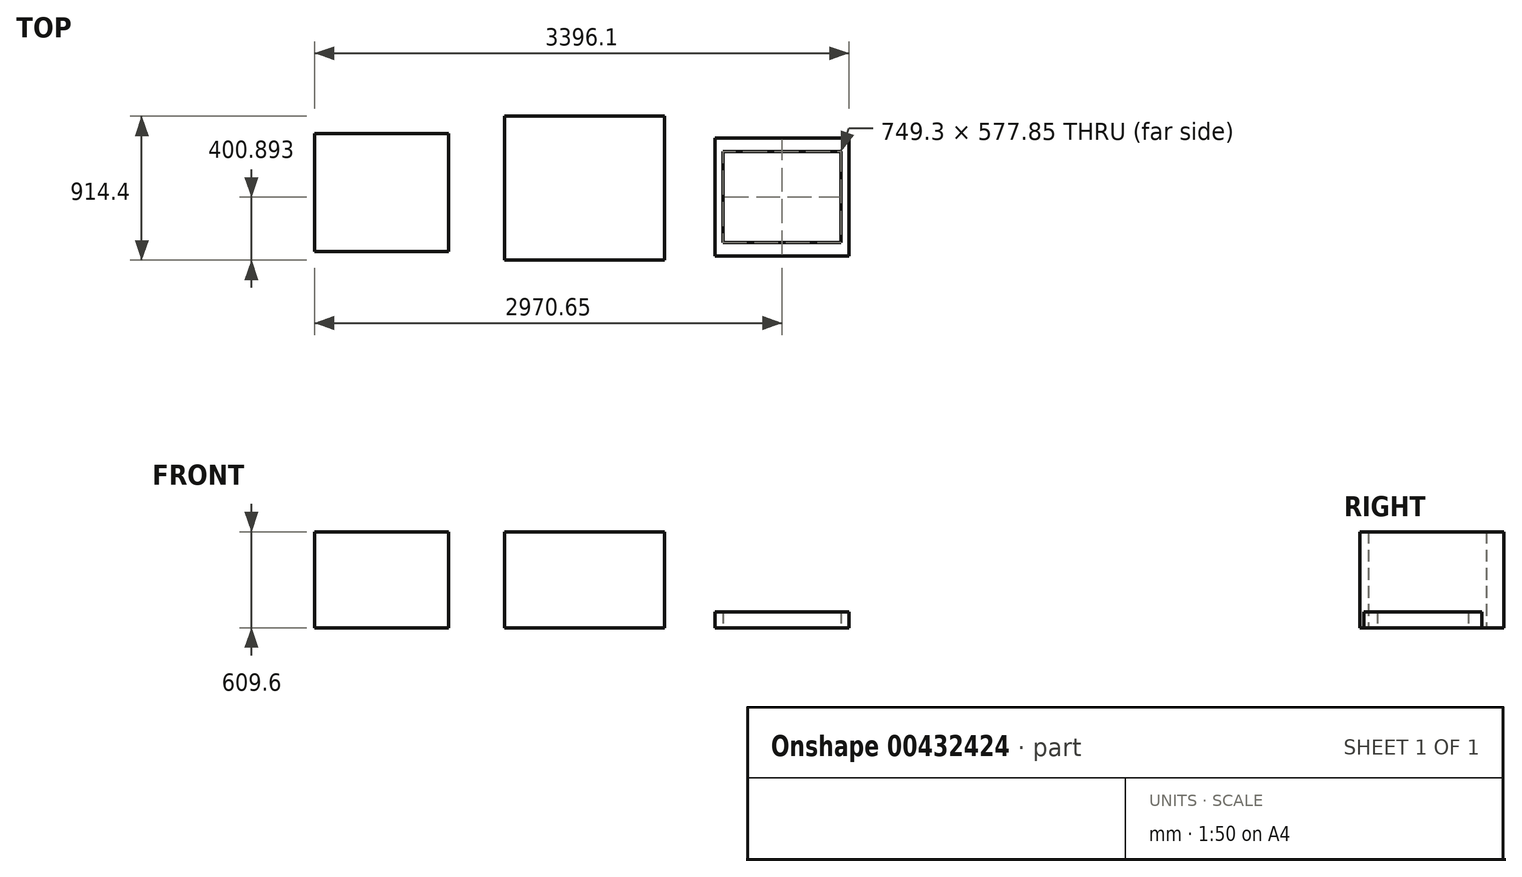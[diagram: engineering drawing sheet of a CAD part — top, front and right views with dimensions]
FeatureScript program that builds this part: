
annotation { "Feature Type Name" : "Feature", "Feature Type Description" : "" }
export const myFeature = defineFeature(function(context is Context, id is Id, definition is map)
    precondition{}
    {
        {
            var Q0;
            Q0=qCreatedBy(makeId("Top.planeOp"),FACE);
            var sketch = newSketch(context, id + "F0", { "sketchPlane" : qUnion([Q0])});
            skLineSegment(sketch, "E0.bottom", {"start": v(-572.13, 395.88) * mm, "end": v(443.87, 395.88) * mm});
            skLineSegment(sketch, "E0.top", {"start": v(-572.13, -518.52) * mm, "end": v(443.87, -518.52) * mm});
            skLineSegment(sketch, "E0.left", {"start": v(-572.13, 395.88) * mm, "end": v(-572.13, -518.52) * mm});
            skLineSegment(sketch, "E0.right", {"start": v(443.87, 395.88) * mm, "end": v(443.87, -518.52) * mm});
            skSolve(sketch);
        }
        {
            var Q0;
            Q0 = qSketchRegion(id + "F0", true);
            extrude(context, id + "F1", {"entities" : qUnion([Q0]), "depth" : 609.6 * mm});
        }
        {
            var Q0;
            Q0=qCreatedBy(makeId("Top.planeOp"),FACE);
            var sketch = newSketch(context, id + "F2", { "sketchPlane" : qUnion([Q0])});
            skLineSegment(sketch, "E1.bottom", {"start": v(-1779.38, 285.49) * mm, "end": v(-928.48, 285.49) * mm});
            skLineSegment(sketch, "E1.top", {"start": v(-1779.38, -463.81) * mm, "end": v(-928.48, -463.81) * mm});
            skLineSegment(sketch, "E1.left", {"start": v(-1779.38, 285.49) * mm, "end": v(-1779.38, -463.81) * mm});
            skLineSegment(sketch, "E1.right", {"start": v(-928.48, 285.49) * mm, "end": v(-928.48, -463.81) * mm});
            skSolve(sketch);
        }
        {
            var Q0;
            Q0=makeQuery(id+"F2.imprint","IMPRINT",FACE,{"disambiguationData":[TD([[makeQuery(id+"F2.imprint","IMPRINT",EDGE,{"derivedFrom":sQuery(id+"F2.wireOp",EDGE,"E1.bottom")}),-1.0]])]});
            extrude(context, id + "F3", {"entities" : qUnion([Q0]), "operationType" : NewBodyOperationType.ADD, "depth" : 609.6 * mm});
        }
        {
            var Q0;
            Q0=qCreatedBy(makeId("Top.planeOp"),FACE);
            var sketch = newSketch(context, id + "F4", { "sketchPlane" : qUnion([Q0])});
            skLineSegment(sketch, "E2.bottom", {"start": v(765.82, 257.02) * mm, "end": v(1616.72, 257.02) * mm});
            skLineSegment(sketch, "E2.top", {"start": v(765.82, -492.28) * mm, "end": v(1616.72, -492.28) * mm});
            skLineSegment(sketch, "E2.left", {"start": v(765.82, 257.02) * mm, "end": v(765.82, -492.28) * mm});
            skLineSegment(sketch, "E2.right", {"start": v(1616.72, 257.02) * mm, "end": v(1616.72, -492.28) * mm});
            skLineSegment(sketch, "E3.bottom", {"start": v(816.62, -406.55) * mm, "end": v(1565.92, -406.55) * mm});
            skLineSegment(sketch, "E3.top", {"start": v(816.62, 171.3) * mm, "end": v(1565.92, 171.3) * mm});
            skLineSegment(sketch, "E3.left", {"start": v(816.62, -406.55) * mm, "end": v(816.62, 171.3) * mm});
            skLineSegment(sketch, "E3.right", {"start": v(1565.92, -406.55) * mm, "end": v(1565.92, 171.3) * mm});
            skSolve(sketch);
        }
        {
            var Q0;
            Q0=makeQuery(id+"F4.imprint","IMPRINT",FACE,{"disambiguationData":[TD([[makeQuery(id+"F4.imprint","IMPRINT",EDGE,{"derivedFrom":sQuery(id+"F4.wireOp",EDGE,"E2.bottom")}),-1.0]])]});
            extrude(context, id + "F5", {"entities" : qUnion([Q0]), "depth" : 101.6 * mm});
        }
    });
